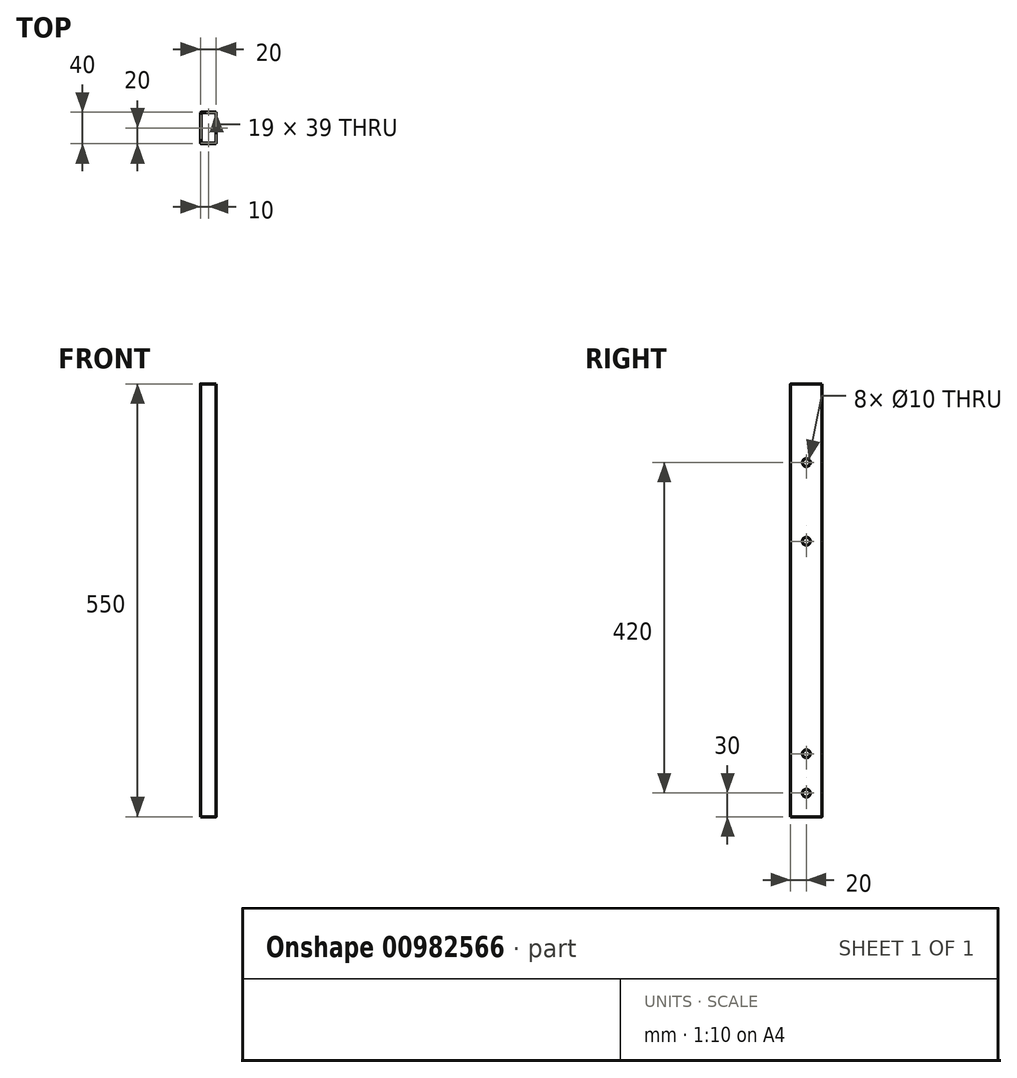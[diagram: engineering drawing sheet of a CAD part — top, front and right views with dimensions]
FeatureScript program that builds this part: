
annotation { "Feature Type Name" : "Feature", "Feature Type Description" : "" }
export const myFeature = defineFeature(function(context is Context, id is Id, definition is map)
    precondition{}
    {
        {
            var Q0;
            Q0=qCreatedBy(makeId("Top.planeOp"),FACE);
            var sketch = newSketch(context, id + "F0", { "sketchPlane" : qUnion([Q0])});
            skLineSegment(sketch, "E0.bottom", {"start": v(-9, 20) * mm, "end": v(9, 20) * mm});
            skLineSegment(sketch, "E0.top", {"start": v(-9, -20) * mm, "end": v(9, -20) * mm});
            skLineSegment(sketch, "E0.left", {"start": v(-10, 19) * mm, "end": v(-10, -19) * mm});
            skLineSegment(sketch, "E0.right", {"start": v(10, 19) * mm, "end": v(10, -19) * mm});
            skPoint(sketch, "E1.visualSharp", {"position": v(-10, 20) * mm});
            skArc(sketch, "E1.filletArc", {"start": v(-9, 20) * mm, "mid": v(-9.7, 19.7) * mm, "end": v(-10, 19) * mm});
            skPoint(sketch, "E2.visualSharp", {"position": v(10, 20) * mm});
            skArc(sketch, "E2.filletArc", {"start": v(10, 19) * mm, "mid": v(9.7, 19.7) * mm, "end": v(9, 20) * mm});
            skPoint(sketch, "E3.visualSharp", {"position": v(10, -20) * mm});
            skArc(sketch, "E3.filletArc", {"start": v(9, -20) * mm, "mid": v(9.7, -19.7) * mm, "end": v(10, -19) * mm});
            skPoint(sketch, "E4.visualSharp", {"position": v(-10, -20) * mm});
            skArc(sketch, "E4.filletArc", {"start": v(-10, -19) * mm, "mid": v(-9.7, -19.7) * mm, "end": v(-9, -20) * mm});
            skLineSegment(sketch, "E5.0", {"start": v(9.5, 19.5) * mm, "end": v(9.5, -19.5) * mm});
            skLineSegment(sketch, "E5.1", {"start": v(-9.5, 19.5) * mm, "end": v(9.5, 19.5) * mm});
            skLineSegment(sketch, "E5.2", {"start": v(-9.5, 19.5) * mm, "end": v(-9.5, -19.5) * mm});
            skLineSegment(sketch, "E5.3", {"start": v(-9.5, -19.5) * mm, "end": v(9.5, -19.5) * mm});
            skSolve(sketch);
        }
        {
            var Q0;
            Q0=makeQuery(id+"F0.imprint","IMPRINT",FACE,{"disambiguationData":[TD([[makeQuery(id+"F0.imprint","IMPRINT",EDGE,{"derivedFrom":sQuery(id+"F0.wireOp",EDGE,"f14a4ae3-e601-47cb-91da-211e3e1e951a.1.0.1")}),-1.0]])]});
            var Q1;
            Q1=makeQuery(id+"F0.imprint","IMPRINT",FACE,{"disambiguationData":[TD([[makeQuery(id+"F0.imprint","IMPRINT",EDGE,{"derivedFrom":sQuery(id+"F0.wireOp",EDGE,"f14a4ae3-e601-47cb-91da-211e3e1e951a.2.0.1")}),-1.0]])]});
            var Q2;
            Q2=makeQuery(id+"F0.imprint","IMPRINT",FACE,{"disambiguationData":[TD([[makeQuery(id+"F0.imprint","IMPRINT",EDGE,{"derivedFrom":sQuery(id+"F0.wireOp",EDGE,"52e9e63f-f607-447c-8eac-f1f637b628d7.1.3.0")}),-1.0]])]});
            var Q3;
            Q3=makeQuery(id+"F0.imprint","IMPRINT",FACE,{"disambiguationData":[TD([[makeQuery(id+"F0.imprint","IMPRINT",EDGE,{"derivedFrom":sQuery(id+"F0.wireOp",EDGE,"E0.bottom")}),-1.0]])]});
            extrude(context, id + "F1", {"entities" : qUnion([Q0, Q1, Q2, Q3]), "depth" : 550 * mm, "offsetDistance" : 25 * mm});
        }
        {
            var Q0;
            Q0=makeQuery(id+"F1.opExtrude","SWEPT_FACE",FACE,{"disambiguationData":[OSD([sQuery(id+"F0.wireOp",EDGE,"E0.right")])]});
            var sketch = newSketch(context, id + "F2", { "sketchPlane" : qUnion([Q0])});
            skPoint(sketch, "E6", {"position": v(0, 30) * mm});
            skPoint(sketch, "E7", {"position": v(0, 80) * mm});
            skPoint(sketch, "E8", {"position": v(0, 450) * mm});
            skPoint(sketch, "E9", {"position": v(0, 350) * mm});
            skSolve(sketch);
        }
        {
            var Q0;
            Q0=sQuery(id+"F2.wireOp",VERTEX,"E7");
            var Q1;
            Q1=sQuery(id+"F2.wireOp",VERTEX,"E6");
            var Q2;
            Q2=sQuery(id+"F2.wireOp",VERTEX,"E8");
            var Q3;
            Q3=sQuery(id+"F2.wireOp",VERTEX,"E9");
            var Q4;
            Q4=makeQuery(id+"F1.opExtrude","SWEPT_BODY",BODY,{"disambiguationData":[OSD([sQuery(id+"F0.wireOp",EDGE,"E0.bottom"),sQuery(id+"F0.wireOp",EDGE,"E0.top"),sQuery(id+"F0.wireOp",EDGE,"E0.left"),sQuery(id+"F0.wireOp",EDGE,"E0.right"),sQuery(id+"F0.wireOp",EDGE,"E1.filletArc"),sQuery(id+"F0.wireOp",EDGE,"E2.filletArc"),sQuery(id+"F0.wireOp",EDGE,"E3.filletArc"),sQuery(id+"F0.wireOp",EDGE,"E4.filletArc"),sQuery(id+"F0.wireOp",EDGE,"E5.0"),sQuery(id+"F0.wireOp",EDGE,"E5.1"),sQuery(id+"F0.wireOp",EDGE,"E5.2"),sQuery(id+"F0.wireOp",EDGE,"E5.3")])]});
            hole(context, id + "F3", {"style" : HoleStyle.SIMPLE, "endStyle" : HoleEndStyle.BLIND, "holeDiameter" : 10 * mm, "majorDiameter" : 5 * mm, "holeDepth" : 30 * mm, "isTappedThrough" : true, "tappedDepth" : 4 * mm, "tapClearance" : 3, "startFromSketch" : true, "locations" : qUnion([Q0, Q1, Q2, Q3]), "scope" : qUnion([Q4])});
        }
    });
